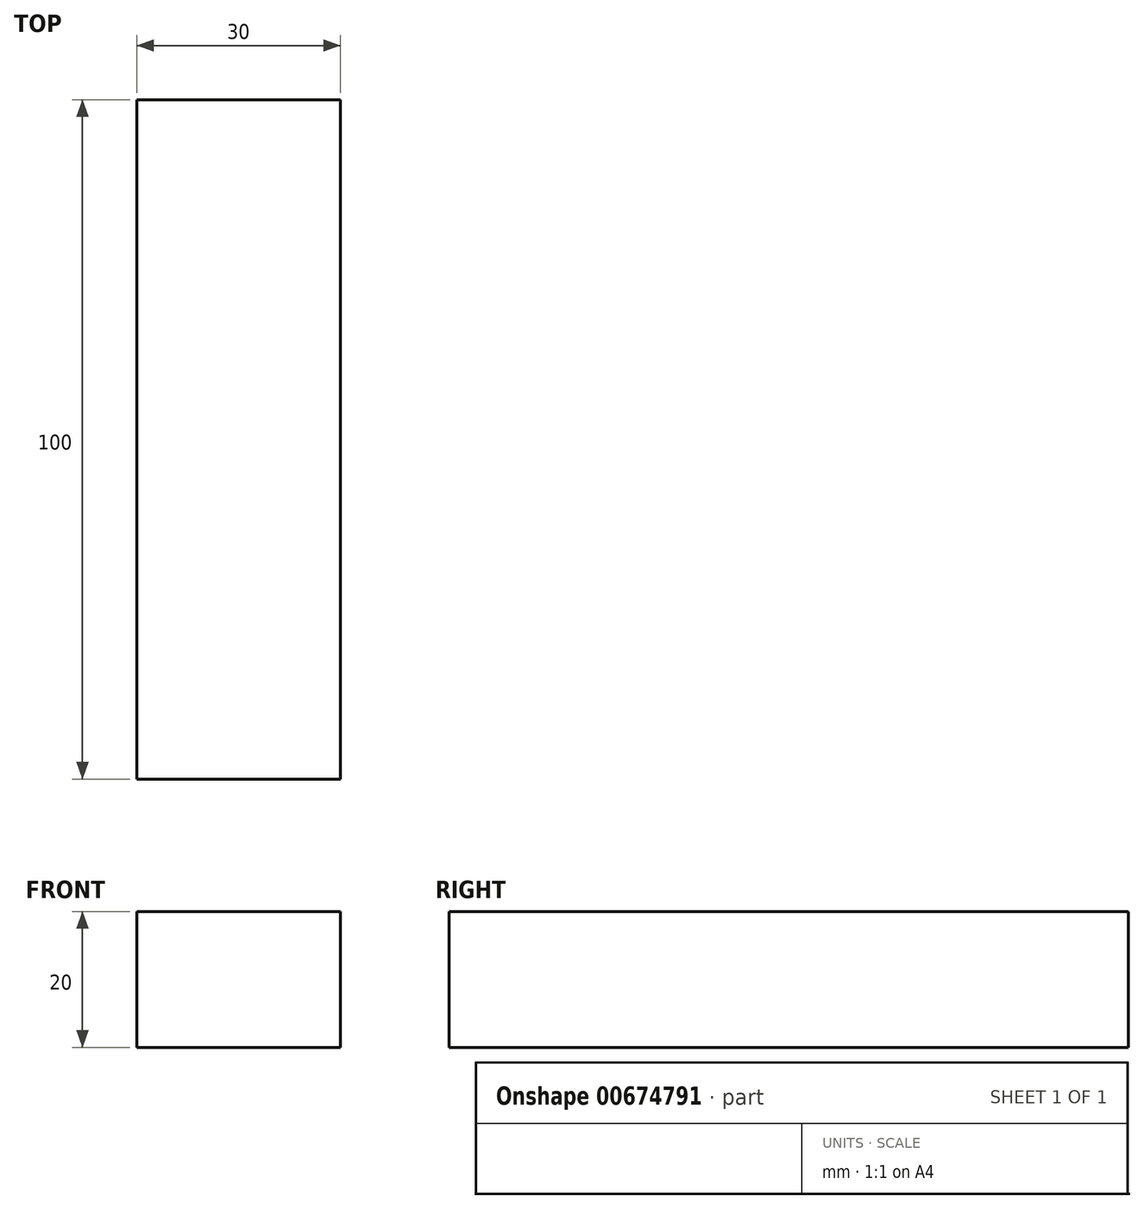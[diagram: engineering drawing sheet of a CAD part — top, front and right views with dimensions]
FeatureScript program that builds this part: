
annotation { "Feature Type Name" : "Feature", "Feature Type Description" : "" }
export const myFeature = defineFeature(function(context is Context, id is Id, definition is map)
    precondition{}
    {
        {
            var Q0;
            Q0=qCreatedBy(makeId("Front.planeOp"),FACE);
            var sketch = newSketch(context, id + "F0", { "sketchPlane" : qUnion([Q0])});
            skLineSegment(sketch, "E0.bottom", {"start": v(15, 10) * mm, "end": v(-15, 10) * mm});
            skLineSegment(sketch, "E0.top", {"start": v(15, -10) * mm, "end": v(-15, -10) * mm});
            skLineSegment(sketch, "E0.left", {"start": v(15, 10) * mm, "end": v(15, -10) * mm});
            skLineSegment(sketch, "E0.right", {"start": v(-15, 10) * mm, "end": v(-15, -10) * mm});
            skPoint(sketch, "E0.middle", {"position": v(0, 0) * mm});
            skSolve(sketch);
        }
        {
            var Q0;
            Q0=makeQuery(id+"F0.imprint","IMPRINT",FACE,{"disambiguationData":[TD([[makeQuery(id+"F0.imprint","IMPRINT",EDGE,{"derivedFrom":sQuery(id+"F0.wireOp",EDGE,"E0.bottom")}),1.0]])]});
            extrude(context, id + "F1", {"entities" : qUnion([Q0]), "endBound" : BoundingType.SYMMETRIC, "depth" : 100 * mm, "offsetDistance" : 25 * mm});
        }
    });
